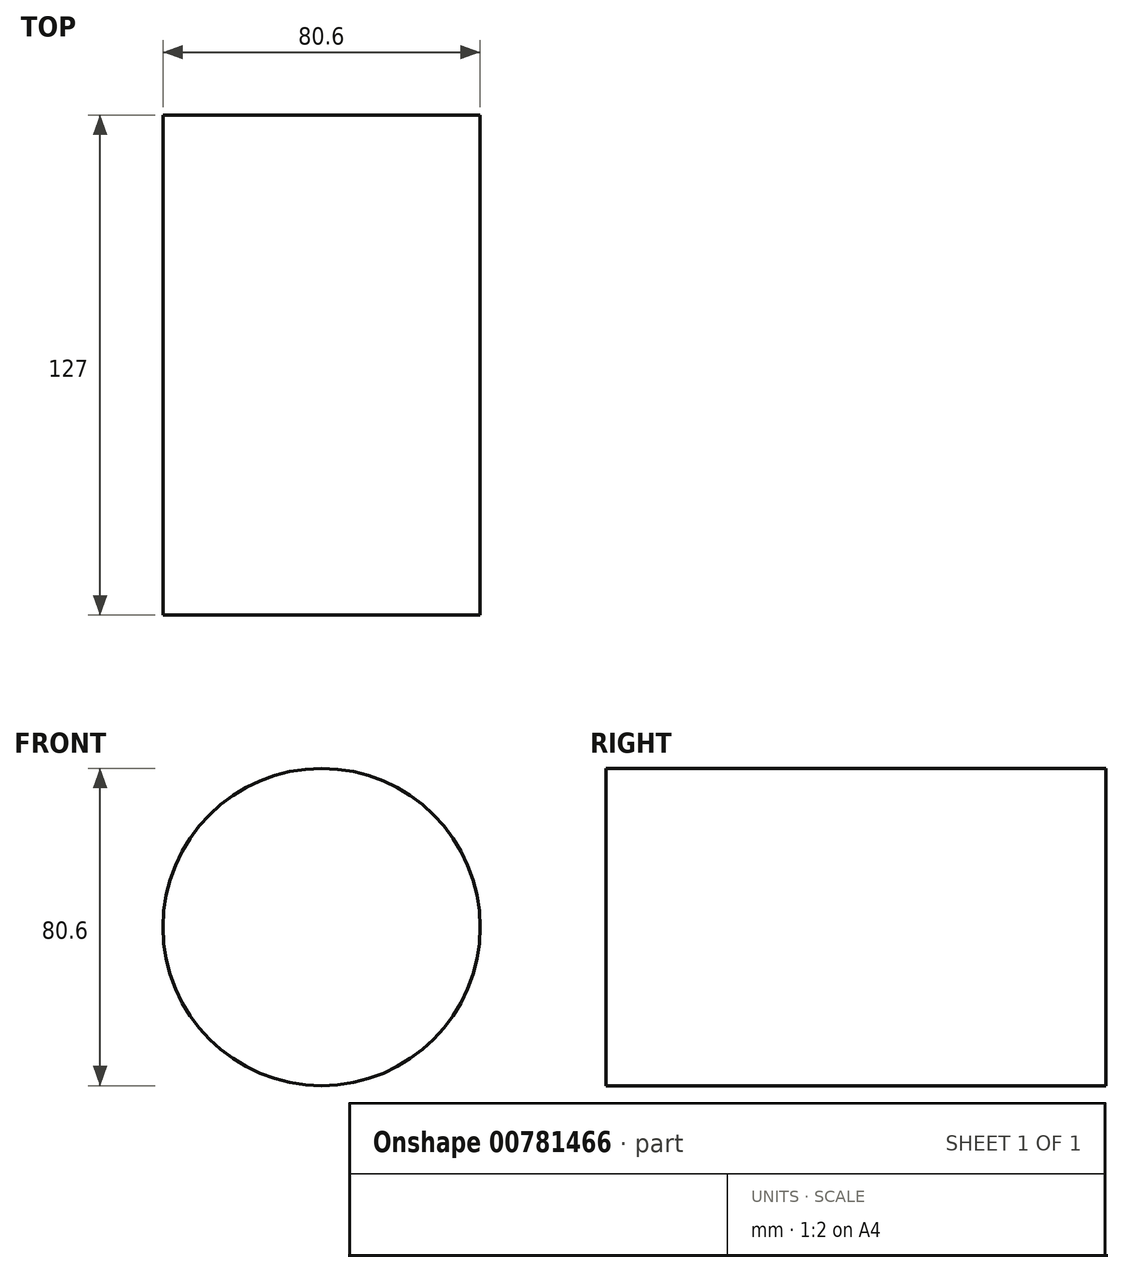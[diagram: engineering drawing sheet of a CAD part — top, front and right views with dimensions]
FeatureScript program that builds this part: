
annotation { "Feature Type Name" : "Feature", "Feature Type Description" : "" }
export const myFeature = defineFeature(function(context is Context, id is Id, definition is map)
    precondition{}
    {
        {
            var Q0;
            Q0=qCreatedBy(makeId("Front.planeOp"),FACE);
            var sketch = newSketch(context, id + "F0", { "sketchPlane" : qUnion([Q0])});
            skCircle(sketch, "E0", {"center": v(0, 0) * mm, "radius": 40.3 * mm});
            skSolve(sketch);
        }
        {
            var Q0;
            Q0=makeQuery(id+"F0.imprint","IMPRINT",FACE,{"disambiguationData":[TD([[makeQuery(id+"F0.imprint","IMPRINT",EDGE,{"derivedFrom":sQuery(id+"F0.wireOp",EDGE,"E0")}),1.0]])]});
            extrude(context, id + "F1", {"entities" : qUnion([Q0]), "depth" : 127 * mm, "offsetDistance" : 25.4 * mm});
        }
    });
